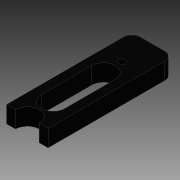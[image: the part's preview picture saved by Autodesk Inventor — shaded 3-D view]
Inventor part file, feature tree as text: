
AUTODESK INVENTOR PART (.ipt)
format: ipt  version: 2015 SP1 (Build 190203100, 203)  size: 98,816 bytes
history: native  units: in
note: dims shown in document units (in); Inventor stores cm internally (conversion verified against a paired STEP export)
features: extrude x1, sketch x1
ambient origin geometry x8: Origin, YZ Plane, XZ Plane, XY Plane, X Axis, Y Axis, Z Axis, Center Point
bodies: Solid1 (feature_tree)
feature tree (2):
  extrude  "Extrusion1"  Depth=1.225in
  sketch  "Sketch1"  dims[d0=3.7in d1=1.225in d2=0.9in d3=0.2in d4=1.5in d5=0.7in d6=0.7in d7=0.25in d8=0.5in d9=0.0in]
